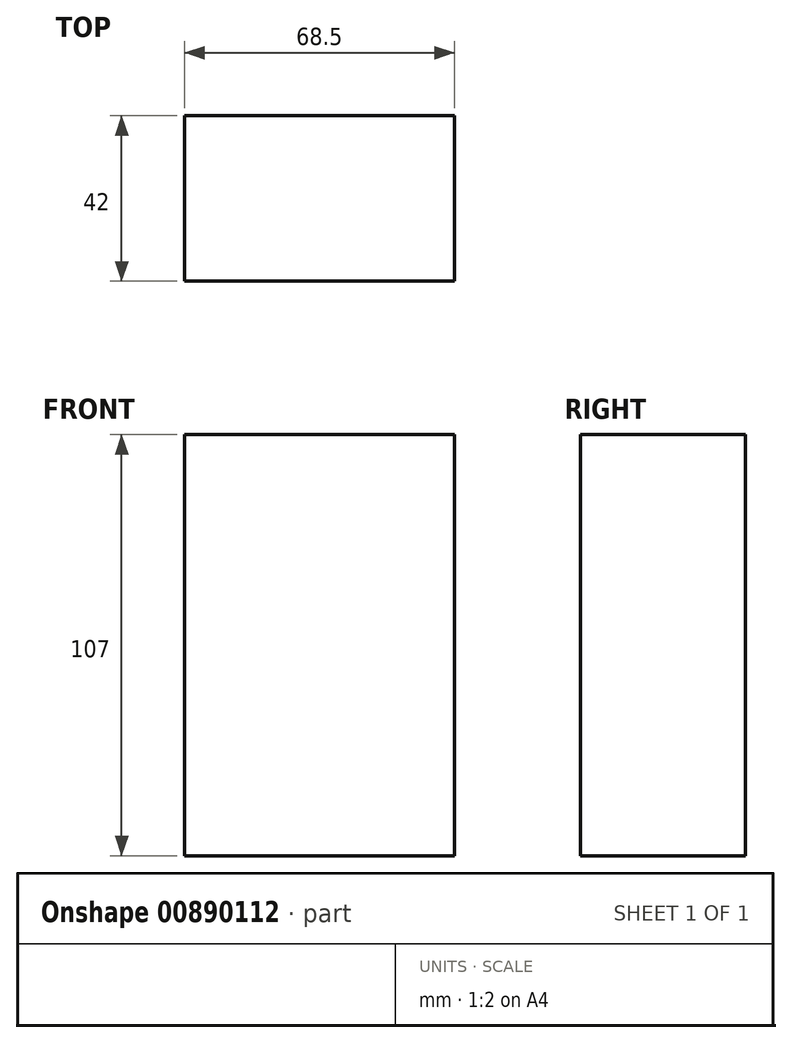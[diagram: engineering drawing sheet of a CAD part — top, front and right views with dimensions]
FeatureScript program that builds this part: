
annotation { "Feature Type Name" : "Feature", "Feature Type Description" : "" }
export const myFeature = defineFeature(function(context is Context, id is Id, definition is map)
    precondition{}
    {
        {
            var Q0;
            Q0=qCreatedBy(makeId("Top.planeOp"),FACE);
            var sketch = newSketch(context, id + "F0", { "sketchPlane" : qUnion([Q0])});
            skLineSegment(sketch, "E0.bottom", {"start": v(-19.67, 38.54) * mm, "end": v(-88.17, 38.54) * mm});
            skLineSegment(sketch, "E0.top", {"start": v(-19.67, 80.54) * mm, "end": v(-88.17, 80.54) * mm});
            skLineSegment(sketch, "E0.left", {"start": v(-19.67, 38.54) * mm, "end": v(-19.67, 80.54) * mm});
            skLineSegment(sketch, "E0.right", {"start": v(-88.17, 38.54) * mm, "end": v(-88.17, 80.54) * mm});
            skPoint(sketch, "E0.middle", {"position": v(-53.92, 59.54) * mm});
            skSolve(sketch);
        }
        {
            var Q0;
            Q0=makeQuery(id+"F0.imprint","IMPRINT",FACE,{"disambiguationData":[TD([[makeQuery(id+"F0.imprint","IMPRINT",EDGE,{"derivedFrom":sQuery(id+"F0.wireOp",EDGE,"E0.bottom")}),-1.0]])]});
            extrude(context, id + "F1", {"entities" : qUnion([Q0]), "depth" : 107 * mm, "offsetDistance" : 25 * mm});
        }
    });
